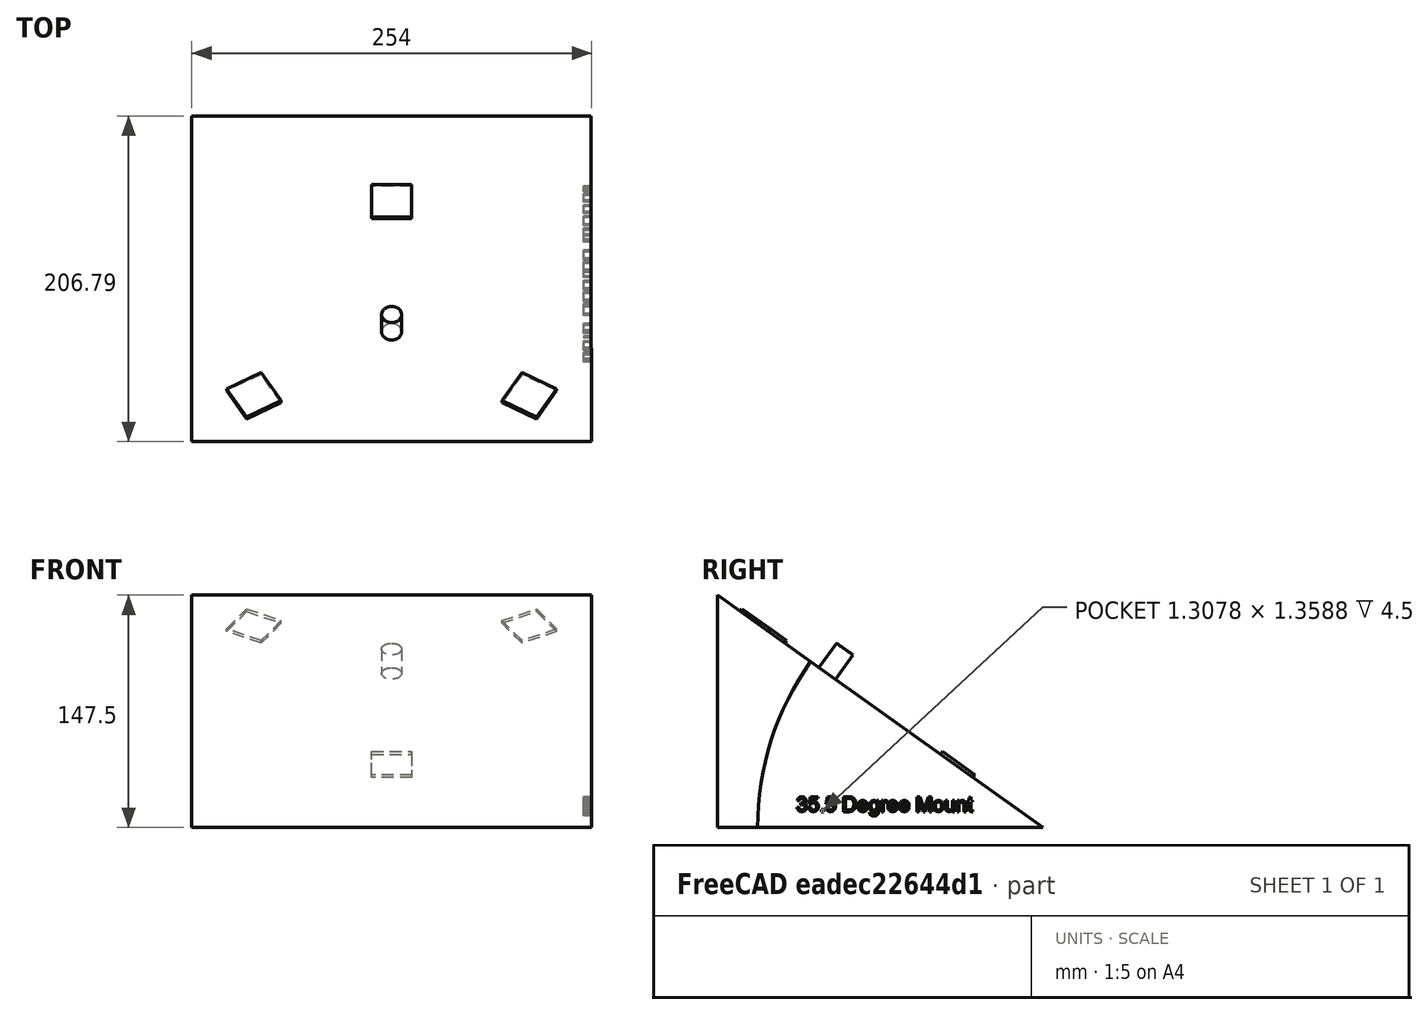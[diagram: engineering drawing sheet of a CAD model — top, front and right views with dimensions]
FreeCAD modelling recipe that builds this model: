
FCSTD DOCUMENT  (FreeCAD 0.19R24291 (Git))
Label: Base35.5Degree
License: All rights reserved
LicenseURL: http://en.wikipedia.org/wiki/All_rights_reserved
objects: TechDraw::DrawViewDimension×8, Sketcher::SketchObject×4, TechDraw::DrawProjGroupItem×4, PartDesign::Pad×3, PartDesign::Pocket×2, TechDraw::DrawSVGTemplate×2, TechDraw::DrawProjGroup×2, TechDraw::DrawPage×2, PartDesign::PolarPattern×1, Part::Part2DObjectPython×1, PartDesign::Body×1
note: 17 computed .brp shape members not serialized (recipe doc carries the construction recipe); baked Part::Feature solids carry a one-line shape summary decoded from their .brp

FEATURE [Sketcher::SketchObject] Sketch
  FullyConstrained = true
  MapMode = 5
  Placement = pos=(0,0,0) rot=(0.57735,0.57735,0.57735;2.0944rad)
  Support = -> [YZ_Plane]
  sketch-geometry (3):
    g0: LineSegment StartX=0 StartY=0 StartZ=0 EndX=206.785 EndY=0 EndZ=0
    g1: LineSegment StartX=206.785 StartY=0 StartZ=0 EndX=0 EndY=147.499 EndZ=0
    g2: LineSegment StartX=0 StartY=147.499 StartZ=0 EndX=0 EndY=0 EndZ=0
  constraints (8):
    c: Coincident(g-1,g0)
    c: Horizontal(g0)
    c: Coincident(g0,g1)
    c: PointOnObject(g1,g-2)
    c: Coincident(g1,g2)
    c: Coincident(g2,g0)
    c: Angle(g1,g0) = 0.619592
    c: Distance(g1) = 254
FEATURE [PartDesign::Pad] Pad  label="PadBase"
  Direction = (1,1,1)
  Length = 254
  Length2 = 100
  Midplane = true
  Placement = pos=(0,0,0) rot=(0.57735,0.57735,0.57735;2.0944rad)
  Profile = -> Sketch
  Type = 0
FEATURE [Sketcher::SketchObject] Sketch001
  FullyConstrained = true
  MapMode = 5
  Placement = pos=(3.6e-15,69.7313,97.7597) rot=(-0.291614,-0.291614,-0.911001;1.66387rad)
  Support = -> [Pad]
  sketch-geometry (1):
    g0: Circle CenterX=0 CenterY=0 CenterZ=0 NormalX=0 NormalY=0 NormalZ=1 AngleXU=0 Radius=6.35
  constraints (2):
    c: Coincident(g0,g-1)
    c: Diameter(g0) = 12.7
FEATURE [PartDesign::Pad] Pad001  label="PadRA_Pin"
  BaseFeature = -> Pad
  Direction = (1,1,1)
  Length = 19.05
  Length2 = 100
  Placement = pos=(0,0,0) rot=(0.57735,0.57735,0.57735;2.0944rad)
  Profile = -> Sketch001
  Type = 0
FEATURE [Sketcher::SketchObject] Sketch002
  FullyConstrained = true
  MapMode = 5
  Placement = pos=(3.6e-15,69.7313,97.7597) rot=(-0.291614,-0.291614,-0.911001;1.66387rad)
  Support = -> [Pad001]
  sketch-geometry (5):
    g0: LineSegment StartX=-88.3 StartY=12.7 StartZ=0 EndX=-113.7 EndY=12.7 EndZ=0
    g1: LineSegment StartX=-113.7 StartY=12.7 StartZ=0 EndX=-113.7 EndY=-12.7 EndZ=0
    g2: LineSegment StartX=-113.7 StartY=-12.7 StartZ=0 EndX=-88.3 EndY=-12.7 EndZ=0
    g3: LineSegment StartX=-88.3 StartY=-12.7 StartZ=0 EndX=-88.3 EndY=12.7 EndZ=0
    g4: GeomPoint X=-101 Y=0 Z=0
  constraints (13):
    c: Coincident(g0,g1)
    c: Coincident(g1,g2)
    c: Coincident(g2,g3)
    c: Coincident(g3,g0)
    c: Horizontal(g0)
    c: Horizontal(g2)
    c: Vertical(g1)
    c: Vertical(g3)
    c: PointOnObject(g4,g-1)
    c: Symmetric(g0,g1,g4)
    c: Equal(g3,g2)
    c: DistanceY(g3,g3) = 25.4
    c: DistanceX(g4,g-1) = 101
FEATURE [PartDesign::Pad] Pad002  label="PadTeflonPad"
  BaseFeature = -> Pad001
  Direction = (1,1,1)
  Length = 2
  Length2 = 100
  Placement = pos=(0,0,0) rot=(0.57735,0.57735,0.57735;2.0944rad)
  Profile = -> Sketch002
  Type = 0
FEATURE [PartDesign::PolarPattern] PolarPattern
  Angle = 360
  Axis = -> Sketch002 [N_Axis]
  BaseFeature = -> Pad002
  Occurrences = 3
  Originals = -> [Pad002]
  Placement = pos=(0,0,0) rot=(0.57735,0.57735,0.57735;2.0944rad)
FEATURE [Part::Part2DObjectPython] ShapeString  # Draft 2D object (typed FeaturePython)
  FontFile = <path>
  Placement = pos=(127,50,10) rot=(0.57735,0.57735,0.57735;2.0944rad)
  Size = 10
  String = 35.5 Degree Mount
  Tracking = 0
FEATURE [PartDesign::Pocket] Pocket
  BaseFeature = -> PolarPattern
  Length = 5
  Length2 = 100
  Placement = pos=(0,0,0) rot=(0.57735,0.57735,0.57735;2.0944rad)
  Profile = -> ShapeString
  Type = 0
FEATURE [Sketcher::SketchObject] Sketch003
  FullyConstrained = false
  MapMode = 5
  Placement = pos=(127,-2.79e-14,2.79e-14) rot=(0.57735,0.57735,0.57735;2.0944rad)
  Support = -> [Pocket]
  sketch-geometry (4):
    g0: ArcOfCircle CenterX=207.298 CenterY=0 CenterZ=0 NormalX=0 NormalY=0 NormalZ=1 AngleXU=0 Radius=181.834 StartAngle=2.52394 EndAngle=3.14159
    g1: LineSegment StartX=59.0596 StartY=105.304 StartZ=0 EndX=59.0911 EndY=105.348 EndZ=0
    g2: LineSegment StartX=59.0911 StartY=105.348 StartZ=0 EndX=207.298 EndY=1.42e-14 EndZ=0
    g3: LineSegment StartX=207.298 StartY=0 StartZ=0 EndX=25.4641 EndY=0 EndZ=0
  constraints (7):
    c: PointOnObject(g0,g-1)
    c: Tangent(g0,g1) = 1.5708
    c: Coincident(g1,g2)
    c: Coincident(g2,g0)
    c: Coincident(g2,g3)
    c: Coincident(g3,g0)
    c: Horizontal(g3)
FEATURE [PartDesign::Pocket] Pocket001
  BaseFeature = -> Pocket
  Length = 0.5
  Length2 = 100
  Placement = pos=(0,0,0) rot=(0.57735,0.57735,0.57735;2.0944rad)
  Profile = -> Sketch003
  Type = 0
FEATURE [PartDesign::Body] Body
  Group = -> [Sketch,Pad,Sketch001,Pad001,Sketch002,Pad002,PolarPattern,ShapeString,Pocket,Sketch003,Pocket001]
  Origin = -> Origin
  Tip = -> Pocket001
FEATURE [TechDraw::DrawSVGTemplate] Template
  Height = 304.8
  Orientation = 1
  Width = 457.2
FEATURE [TechDraw::DrawProjGroupItem] ProjItem  label="Front"
  CoarseView = false
  Direction = (1,0,0)
  Focus = 100
  HardHidden = false
  IsoCount = 0
  IsoHidden = false
  IsoVisible = false
  LockPosition = true
  Perspective = false
  Rotation = 0
  RotationVector = (0,1,0)
  Scale = 0.5
  ScaleType = 2
  SeamHidden = false
  SeamVisible = true
  SmoothHidden = false
  SmoothVisible = true
  Source = -> [Body]
  Type = 0
  X = 0
  XDirection = (0,1,0)
  Y = 0
FEATURE [TechDraw::DrawProjGroupItem] ProjItem001  label="Bottom"
  CoarseView = false
  Direction = (0,0,-1)
  Focus = 100
  HardHidden = false
  IsoCount = 0
  IsoHidden = false
  IsoVisible = false
  LockPosition = true
  Perspective = false
  Rotation = 0
  RotationVector = (1,0,0)
  Scale = 0.5
  ScaleType = 2
  SeamHidden = false
  SeamVisible = true
  SmoothHidden = false
  SmoothVisible = true
  Source = -> [Body]
  Type = 5
  X = 0
  XDirection = (0,1,0)
  Y = 132.555
FEATURE [TechDraw::DrawProjGroupItem] ProjItem002  label="FrontTopRight"
  CoarseView = false
  Direction = (0.57735,0.57735,0.57735)
  Focus = 100
  HardHidden = false
  IsoCount = 0
  IsoHidden = false
  IsoVisible = false
  LockPosition = true
  Perspective = false
  Rotation = 0
  RotationVector = (1,0,0)
  ScaleType = 2
  SeamHidden = false
  SeamVisible = true
  SmoothHidden = false
  SmoothVisible = true
  Source = -> [Body]
  Type = 7
  X = 203.644
  XDirection = (-0.707107,0.707107,0)
  Y = 99.6804
FEATURE [TechDraw::DrawProjGroup] ProjGroup
  Anchor = -> ProjItem
  AutoDistribute = true
  LockPosition = false
  ProjectionType = 0
  Rotation = 0
  Scale = 0.5
  ScaleType = 2
  Source = -> [Body]
  Views = -> [ProjItem,ProjItem001,ProjItem002]
  X = 104.206
  Y = 71.5146
  spacingX = 15.0114
  spacingY = 15.0114
FEATURE [TechDraw::DrawViewDimension] Dimension
  Arbitrary = false
  ArbitraryTolerances = false
  EqualTolerance = true
  FormatSpec = %.3f
  FormatSpecOverTolerance = %+.3f
  FormatSpecUnderTolerance = %+.3f
  Inverted = false
  LockPosition = false
  MeasureType = 1
  OverTolerance = 0
  References2D = -> [ProjItem001]
  Rotation = 0
  ScaleType = 2
  TheoreticalExact = false
  Type = 1
  UnderTolerance = 0
  X = 0.411003
  Y = -80.7621
FEATURE [TechDraw::DrawViewDimension] Dimension001
  Arbitrary = false
  ArbitraryTolerances = false
  EqualTolerance = true
  FormatSpec = %.3f
  FormatSpecOverTolerance = %+.3f
  FormatSpecUnderTolerance = %+.3f
  Inverted = false
  LockPosition = false
  MeasureType = 1
  OverTolerance = 0
  References2D = -> [ProjItem001]
  Rotation = 0
  ScaleType = 2
  TheoreticalExact = false
  Type = 2
  UnderTolerance = 0
  X = 59.9506
  Y = 2.12616
FEATURE [TechDraw::DrawPage] Page
  KeepUpdated = true
  NextBalloonIndex = 1
  ProjectionType = 0
  Template = -> Template
  Views = -> [ProjGroup,Dimension,Dimension001]
FEATURE [TechDraw::DrawSVGTemplate] Template001
  Height = 304.8
  Orientation = 1
  Width = 457.2
FEATURE [TechDraw::DrawProjGroupItem] ProjItem003  label="Front001"
  CoarseView = false
  Direction = (-0.026,0.439,0.898)
  Focus = 100
  HardHidden = false
  IsoCount = 0
  IsoHidden = false
  IsoVisible = false
  LockPosition = true
  Perspective = false
  Rotation = 0
  RotationVector = (-1,-0.006,-0.027)
  Scale = 0.5
  ScaleType = 2
  SeamHidden = false
  SeamVisible = true
  SmoothHidden = false
  SmoothVisible = true
  Source = -> [Body]
  Type = 0
  X = 0
  XDirection = (-1,-0.006,-0.027)
  Y = 0
FEATURE [TechDraw::DrawProjGroup] ProjGroup001
  Anchor = -> ProjItem003
  AutoDistribute = true
  LockPosition = false
  ProjectionType = 0
  Rotation = 0
  Scale = 0.5
  ScaleType = 2
  Source = -> [Body]
  Views = -> [ProjItem003]
  X = 146.443
  Y = 156.134
  spacingX = 15.0114
  spacingY = 15.0114
FEATURE [TechDraw::DrawViewDimension] Dimension002
  Arbitrary = false
  ArbitraryTolerances = false
  EqualTolerance = true
  FormatSpec = %.3f
  FormatSpecOverTolerance = %+.3f
  FormatSpecUnderTolerance = %+.3f
  Inverted = false
  LockPosition = false
  MeasureType = 1
  OverTolerance = 0
  References2D = -> [ProjItem003]
  Rotation = 0
  ScaleType = 2
  TheoreticalExact = false
  Type = 1
  UnderTolerance = 0
  X = 0.961103
  Y = -102.256
FEATURE [TechDraw::DrawViewDimension] Dimension003
  Arbitrary = false
  ArbitraryTolerances = false
  EqualTolerance = true
  FormatSpec = %.3f
  FormatSpecOverTolerance = %+.3f
  FormatSpecUnderTolerance = %+.3f
  Inverted = false
  LockPosition = false
  MeasureType = 1
  OverTolerance = 0
  References2D = -> [ProjItem003]
  Rotation = 0
  ScaleType = 2
  TheoreticalExact = false
  Type = 2
  UnderTolerance = 0
  X = 80.0268
  Y = 1.8367
FEATURE [TechDraw::DrawViewDimension] Dimension004
  Arbitrary = false
  ArbitraryTolerances = false
  EqualTolerance = true
  FormatSpec = %.3f
  FormatSpecOverTolerance = %+.3f
  FormatSpecUnderTolerance = %+.3f
  Inverted = false
  LockPosition = false
  MeasureType = 1
  OverTolerance = 0
  References2D = -> [ProjItem003]
  Rotation = 0
  ScaleType = 2
  TheoreticalExact = false
  Type = 1
  UnderTolerance = 0
  X = -51.882
  Y = 26.8776
FEATURE [TechDraw::DrawViewDimension] Dimension005
  Arbitrary = false
  ArbitraryTolerances = false
  EqualTolerance = true
  FormatSpec = %.3f
  FormatSpecOverTolerance = %+.3f
  FormatSpecUnderTolerance = %+.3f
  Inverted = false
  LockPosition = false
  MeasureType = 1
  OverTolerance = 0
  References2D = -> [ProjItem003]
  Rotation = 0
  ScaleType = 2
  TheoreticalExact = false
  Type = 2
  UnderTolerance = 0
  X = -84.5321
  Y = -19.5329
FEATURE [TechDraw::DrawViewDimension] Dimension006
  Arbitrary = false
  ArbitraryTolerances = false
  EqualTolerance = true
  FormatSpec = %.3f
  FormatSpecOverTolerance = %+.3f
  FormatSpecUnderTolerance = %+.3f
  Inverted = false
  LockPosition = false
  MeasureType = 1
  OverTolerance = 0
  References2D = -> [ProjItem003]
  Rotation = 0
  ScaleType = 2
  TheoreticalExact = false
  Type = 2
  UnderTolerance = 0
  X = 10.24
  Y = -53.5777
FEATURE [TechDraw::DrawViewDimension] Dimension007
  Arbitrary = false
  ArbitraryTolerances = false
  EqualTolerance = true
  FormatSpec = %.3f
  FormatSpecOverTolerance = %+.3f
  FormatSpecUnderTolerance = %+.3f
  Inverted = false
  LockPosition = false
  MeasureType = 1
  OverTolerance = 0
  References2D = -> [ProjItem003]
  Rotation = 0
  ScaleType = 2
  TheoreticalExact = false
  Type = 1
  UnderTolerance = 0
  X = -35.3813
  Y = -34.2606
FEATURE [TechDraw::DrawPage] Page001
  KeepUpdated = true
  NextBalloonIndex = 1
  ProjectionType = 0
  Template = -> Template001
  Views = -> [ProjGroup001,Dimension002,Dimension003,Dimension004,Dimension005,Dimension006,Dimension007]
note: 1 file-system path scrubbed to <path> (originals preserved in the JSON sidecar)
